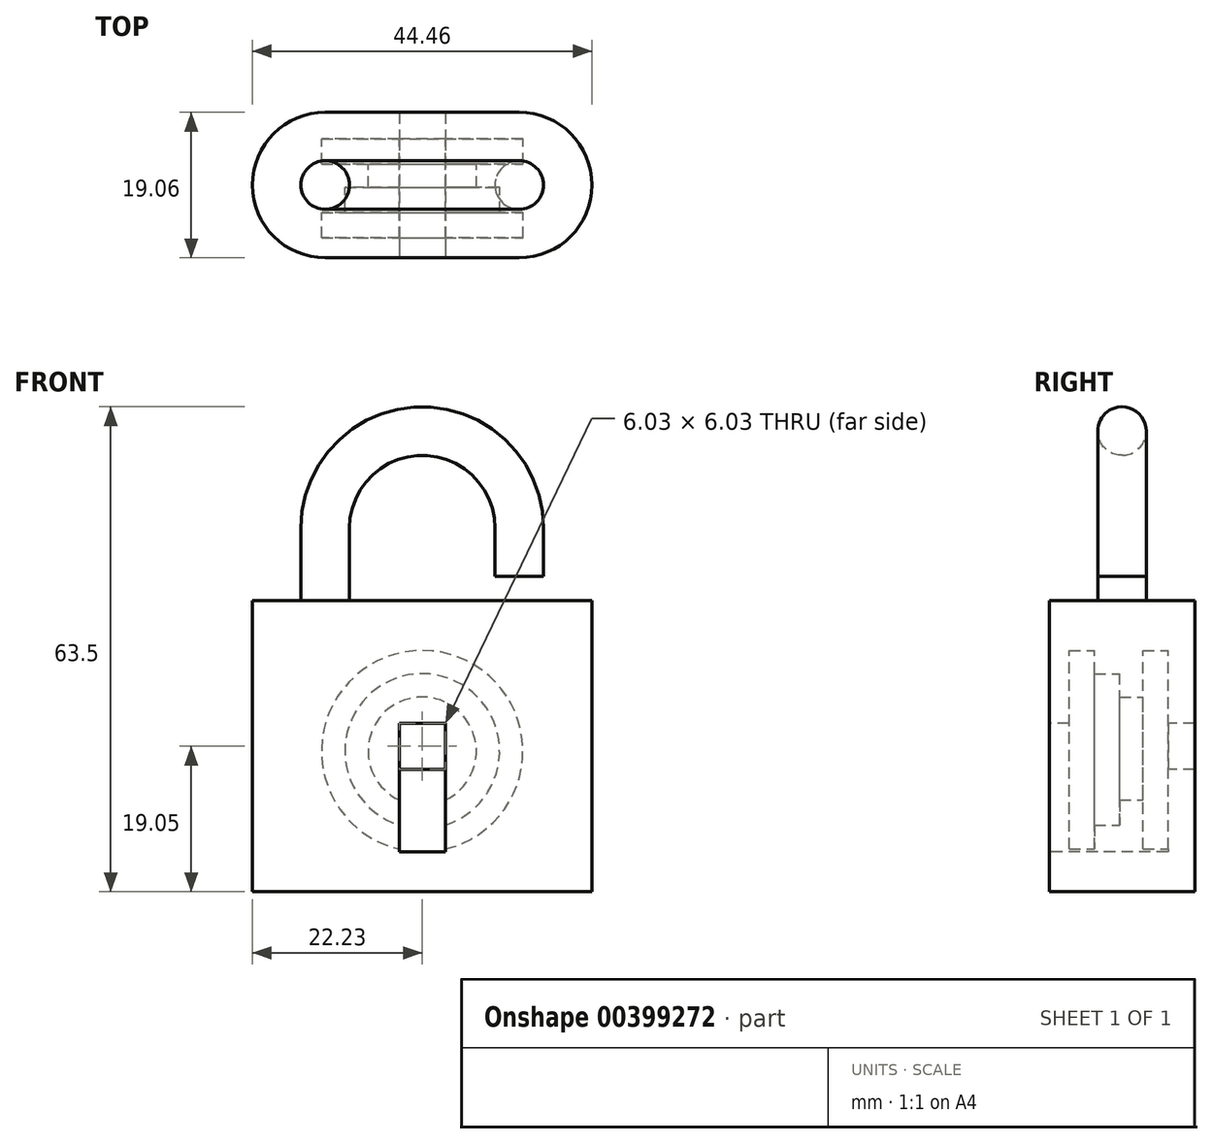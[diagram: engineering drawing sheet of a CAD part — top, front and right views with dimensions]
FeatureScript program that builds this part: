
annotation { "Feature Type Name" : "Feature", "Feature Type Description" : "" }
export const myFeature = defineFeature(function(context is Context, id is Id, definition is map)
    precondition{}
    {
        {
            var Q0;
            Q0=qCreatedBy(makeId("Top.planeOp"),FACE);
            var sketch = newSketch(context, id + "F0", { "sketchPlane" : qUnion([Q0])});
            skLineSegment(sketch, "E0.bottom", {"start": v(12.7, 9.53) * mm, "end": v(-12.7, 9.53) * mm});
            skLineSegment(sketch, "E0.top", {"start": v(12.7, -9.52) * mm, "end": v(-12.7, -9.52) * mm});
            skPoint(sketch, "E0.middle", {"position": v(0, 0) * mm});
            skArc(sketch, "E1", {"start": v(-12.7, 9.53) * mm, "mid": v(-22.23, 0) * mm, "end": v(-12.7, -9.53) * mm});
            skArc(sketch, "E2", {"start": v(12.7, 9.53) * mm, "mid": v(22.23, 0) * mm, "end": v(12.7, -9.52) * mm});
            skSolve(sketch);
        }
        {
            var Q0;
            Q0 = qSketchRegion(id + "F0", true);
            extrude(context, id + "F1", {"entities" : qUnion([Q0]), "depth" : 38.1 * mm});
        }
        {
            var Q0;
            Q0=makeQuery(id+"F1.opExtrude","SWEPT_FACE",FACE,{"disambiguationData":[OSD([sQuery(id+"F0.wireOp",EDGE,"E0.top")])]});
            var sketch = newSketch(context, id + "F2", { "sketchPlane" : qUnion([Q0])});
            skLineSegment(sketch, "E3.bottom", {"start": v(3.02, 22.07) * mm, "end": v(-3.02, 22.07) * mm});
            skLineSegment(sketch, "E3.top", {"start": v(3.02, 16.03) * mm, "end": v(-3.02, 16.03) * mm});
            skLineSegment(sketch, "E3.left", {"start": v(3.02, 22.07) * mm, "end": v(3.02, 16.03) * mm});
            skLineSegment(sketch, "E3.right", {"start": v(-3.02, 22.07) * mm, "end": v(-3.02, 16.03) * mm});
            skPoint(sketch, "E3.middle", {"position": v(0, 19.05) * mm});
            skSolve(sketch);
        }
        {
            var Q0;
            Q0 = qSketchRegion(id + "F2", true);
            extrude(context, id + "F3", {"entities" : qUnion([Q0]), "operationType" : NewBodyOperationType.REMOVE, "endBound" : BoundingType.THROUGH_ALL, "oppositeDirection" : true, "depth" : 15.88 * mm});
        }
        {
            var Q0;
            Q0=makeQuery(id+"F1.opExtrude","SWEPT_FACE",FACE,{"disambiguationData":[OSD([sQuery(id+"F0.wireOp",EDGE,"E0.top")])]});
            var sketch = newSketch(context, id + "F4", { "sketchPlane" : qUnion([Q0])});
            skLineSegment(sketch, "E4.bottom", {"start": v(-3.02, 16.03) * mm, "end": v(3.02, 16.03) * mm});
            skLineSegment(sketch, "E4.top", {"start": v(-3.02, 5.24) * mm, "end": v(3.02, 5.24) * mm});
            skLineSegment(sketch, "E4.left", {"start": v(-3.02, 16.03) * mm, "end": v(-3.02, 5.24) * mm});
            skLineSegment(sketch, "E4.right", {"start": v(3.02, 16.03) * mm, "end": v(3.02, 5.24) * mm});
            skSolve(sketch);
        }
        {
            var Q0;
            Q0 = qSketchRegion(id + "F4", true);
            extrude(context, id + "F5", {"entities" : qUnion([Q0]), "operationType" : NewBodyOperationType.REMOVE, "oppositeDirection" : true, "depth" : 15.56 * mm});
        }
        {
            var Q0;
            Q0=qCreatedBy(makeId("Right.planeOp"),FACE);
            var sketch = newSketch(context, id + "F6", { "sketchPlane" : qUnion([Q0])});
            skLineSegment(sketch, "E5", {"start": v(6.03, 18.41) * mm, "end": v(6.03, 5.24) * mm});
            skLineSegment(sketch, "E6", {"start": v(6.03, 5.24) * mm, "end": v(2.73, 5.24) * mm});
            skLineSegment(sketch, "E7", {"start": v(-6.92, 18.41) * mm, "end": v(6.03, 18.41) * mm});
            skLineSegment(sketch, "E8", {"start": v(2.73, 5.24) * mm, "end": v(2.73, 11.33) * mm});
            skLineSegment(sketch, "E9", {"start": v(2.73, 11.33) * mm, "end": v(-0.32, 11.33) * mm});
            skLineSegment(sketch, "E10", {"start": v(-0.32, 11.33) * mm, "end": v(-0.32, 8.29) * mm});
            skLineSegment(sketch, "E11", {"start": v(-0.32, 8.29) * mm, "end": v(-3.62, 8.29) * mm});
            skLineSegment(sketch, "E12", {"start": v(-3.62, 8.29) * mm, "end": v(-3.62, 5.24) * mm});
            skLineSegment(sketch, "E13", {"start": v(-3.62, 5.24) * mm, "end": v(-6.92, 5.24) * mm});
            skLineSegment(sketch, "E14", {"start": v(-6.92, 5.24) * mm, "end": v(-6.92, 18.41) * mm});
            skSolve(sketch);
        }
        {
            var Q0;
            Q0 = qSketchRegion(id + "F6", true);
            var Q1;
            Q1=sQuery(id+"F6.wireOp",EDGE,"E7");
            revolve(context, id + "F7", {"operationType" : NewBodyOperationType.REMOVE, "entities" : qUnion([Q0]), "axis" : qUnion([Q1]), "revolveType" : RevolveType.FULL, "oppositeDirection" : true});
        }
        {
            var Q0;
            Q0=makeQuery(id+"F1.opExtrude","CAP_FACE",FACE,{"disambiguationData":[OSD([sQuery(id+"F0.wireOp",EDGE,"E0.bottom"),sQuery(id+"F0.wireOp",EDGE,"E0.top"),sQuery(id+"F0.wireOp",EDGE,"E1"),sQuery(id+"F0.wireOp",EDGE,"E2")])],"isStart":false});
            var sketch = newSketch(context, id + "F8", { "sketchPlane" : qUnion([Q0])});
            skCircle(sketch, "E15", {"center": v(-12.7, 0) * mm, "radius": 3.18 * mm});
            skSolve(sketch);
        }
        {
            var Q0;
            Q0=qCreatedBy(makeId("Front.planeOp"),FACE);
            var sketch = newSketch(context, id + "F9", { "sketchPlane" : qUnion([Q0])});
            skLineSegment(sketch, "E16", {"start": v(-12.7, 38.1) * mm, "end": v(-12.7, 47.62) * mm});
            skLineSegment(sketch, "E17", {"start": v(12.7, 41.27) * mm, "end": v(12.7, 47.62) * mm});
            skArc(sketch, "E18", {"start": v(-12.7, 47.62) * mm, "mid": v(0, 60.33) * mm, "end": v(12.7, 47.62) * mm});
            skSolve(sketch);
        }
        {
            var Q0;
            Q0 = qSketchRegion(id + "F8", true);
            var Q1;
            Q1 = qConstructionFilter(qBodyType(qCreatedBy(id + "F9" ,EDGE), BodyType.WIRE), ConstructionObject.NO);
            sweep(context, id + "F10", {"operationType" : NewBodyOperationType.ADD, "profiles" : qUnion([Q0]), "path" : qUnion([Q1])});
        }
    });
